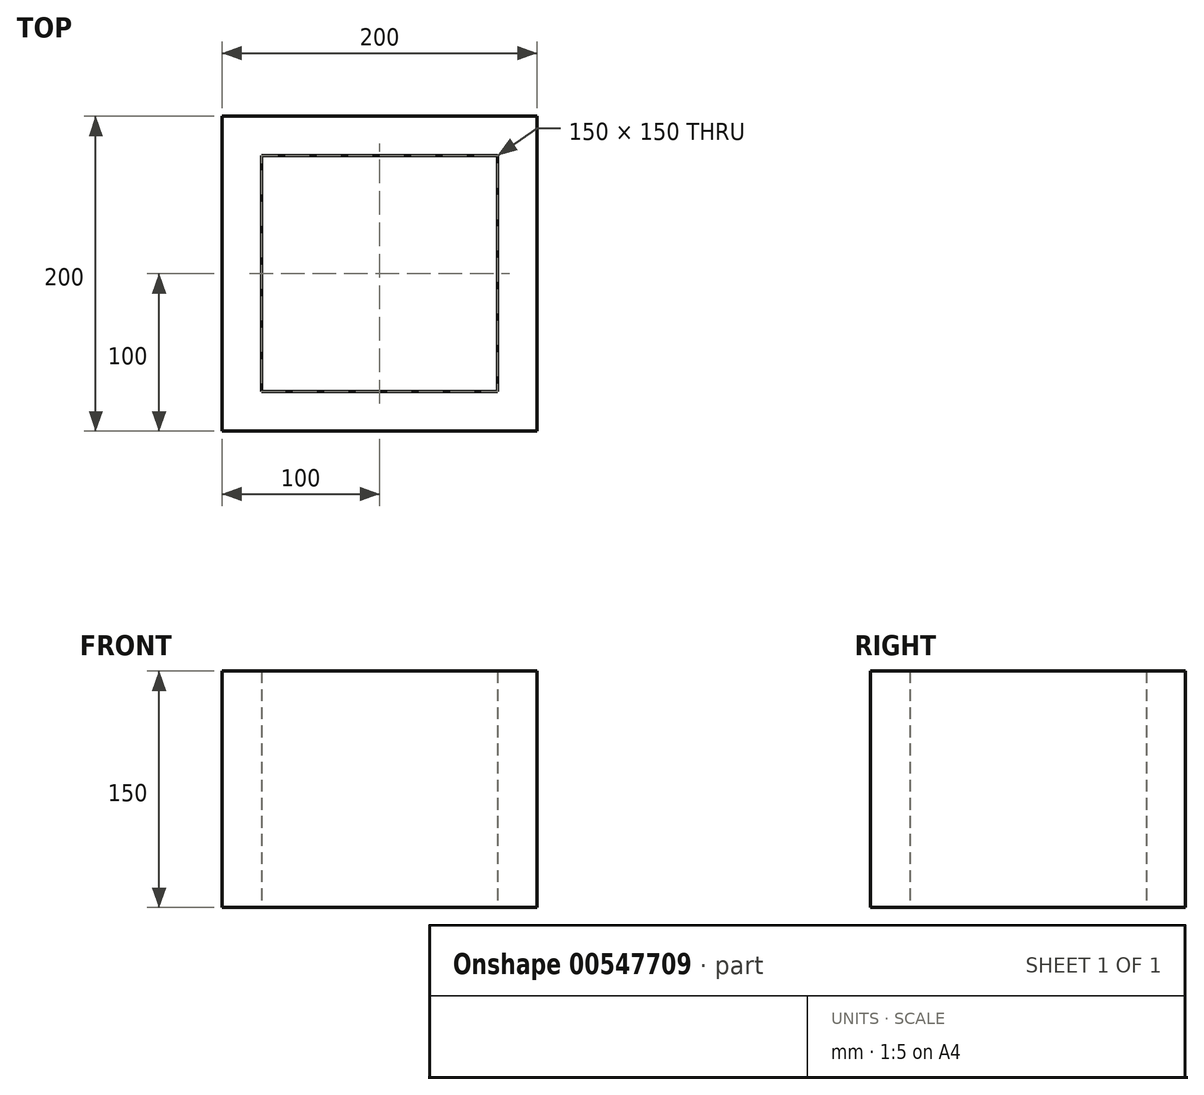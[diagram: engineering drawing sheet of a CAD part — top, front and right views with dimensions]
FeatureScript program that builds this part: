
annotation { "Feature Type Name" : "Feature", "Feature Type Description" : "" }
export const myFeature = defineFeature(function(context is Context, id is Id, definition is map)
    precondition{}
    {
        {
            var Q0;
            Q0=qCreatedBy(makeId("Top.planeOp"),FACE);
            var sketch = newSketch(context, id + "F0", { "sketchPlane" : qUnion([Q0])});
            skLineSegment(sketch, "E0.bottom", {"start": v(100, 100) * mm, "end": v(-100, 100) * mm});
            skLineSegment(sketch, "E0.top", {"start": v(100, -100) * mm, "end": v(-100, -100) * mm});
            skLineSegment(sketch, "E0.left", {"start": v(100, 100) * mm, "end": v(100, -100) * mm});
            skLineSegment(sketch, "E0.right", {"start": v(-100, 100) * mm, "end": v(-100, -100) * mm});
            skPoint(sketch, "E0.middle", {"position": v(0, 0) * mm});
            skLineSegment(sketch, "E1.bottom", {"start": v(75, 75) * mm, "end": v(-75, 75) * mm});
            skLineSegment(sketch, "E1.top", {"start": v(75, -75) * mm, "end": v(-75, -75) * mm});
            skLineSegment(sketch, "E1.left", {"start": v(75, 75) * mm, "end": v(75, -75) * mm});
            skLineSegment(sketch, "E1.right", {"start": v(-75, 75) * mm, "end": v(-75, -75) * mm});
            skSolve(sketch);
        }
        {
            var Q0;
            Q0 = qSketchRegion(id + "F0", true);
            extrude(context, id + "F1", {"entities" : qUnion([Q0]), "depth" : 150 * mm, "offsetDistance" : 25 * mm});
        }
    });
